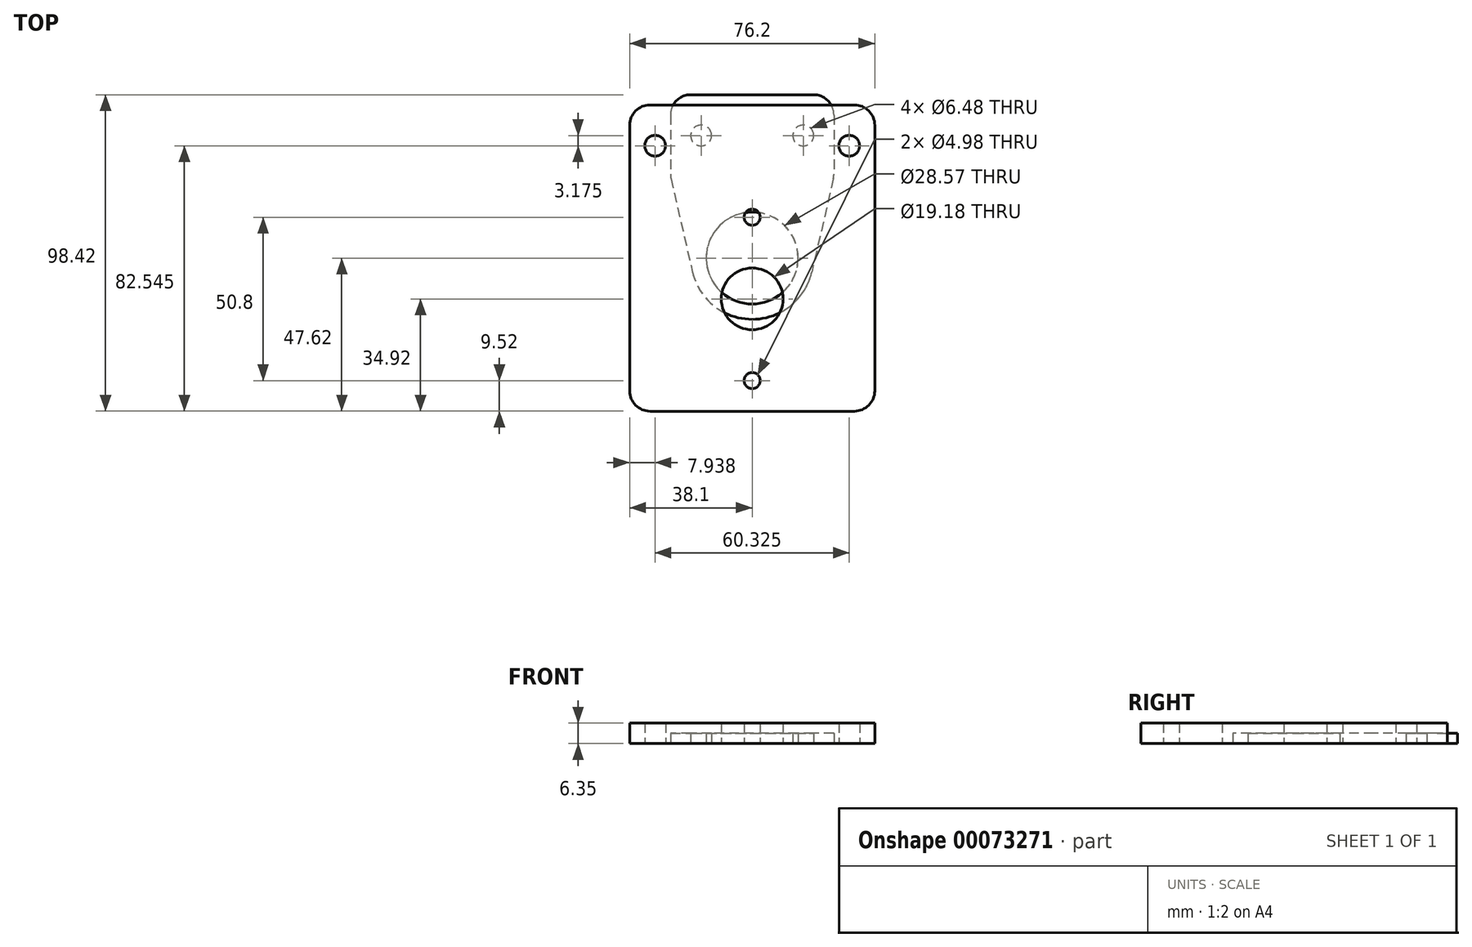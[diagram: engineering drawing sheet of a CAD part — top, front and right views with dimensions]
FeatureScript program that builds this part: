
annotation { "Feature Type Name" : "Feature", "Feature Type Description" : "" }
export const myFeature = defineFeature(function(context is Context, id is Id, definition is map)
    precondition{}
    {
        {
            var Q0;
            Q0=qCreatedBy(makeId("Top.planeOp"),FACE);
            var sketch = newSketch(context, id + "F0", { "sketchPlane" : qUnion([Q0])});
            skLineSegment(sketch, "E0.rect.bottom", {"start": v(38.1, 47.62) * mm, "end": v(-38.1, 47.62) * mm});
            skLineSegment(sketch, "E0.rect.top", {"start": v(38.1, -47.63) * mm, "end": v(-38.1, -47.63) * mm});
            skLineSegment(sketch, "E0.rect.left", {"start": v(38.1, 47.63) * mm, "end": v(38.1, -47.63) * mm});
            skLineSegment(sketch, "E0.rect.right", {"start": v(-38.1, 47.63) * mm, "end": v(-38.1, -47.63) * mm});
            skPoint(sketch, "E0.rect.middle", {"position": v(0, 0) * mm});
            skLineSegment(sketch, "E1", {"start": v(-38.1, 22.22) * mm, "end": v(38.1, 22.23) * mm, "construction": true});
            skLineSegment(sketch, "E2", {"start": v(0, 47.62) * mm, "end": v(0, -47.63) * mm, "construction": true});
            skLineSegment(sketch, "E3", {"start": v(-38.1, 34.92) * mm, "end": v(38.1, 34.92) * mm, "construction": true});
            skCircle(sketch, "E4", {"center": v(-30.16, 34.92) * mm, "radius": 3.24 * mm});
            skCircle(sketch, "E5", {"center": v(30.16, 34.92) * mm, "radius": 3.24 * mm});
            skCircle(sketch, "E6", {"center": v(0, -12.7) * mm, "radius": 9.59 * mm});
            skCircle(sketch, "E7", {"center": v(0, -12.7) * mm, "radius": 32.39 * mm, "construction": true});
            skCircle(sketch, "E8", {"center": v(0, -12.7) * mm, "radius": 25.4 * mm, "construction": true});
            skCircle(sketch, "E9", {"center": v(0, 12.7) * mm, "radius": 2.49 * mm});
            skCircle(sketch, "E10", {"center": v(0, -38.1) * mm, "radius": 2.49 * mm});
            skLineSegment(sketch, "E11", {"start": v(-32.39, -12.7) * mm, "end": v(32.39, -12.7) * mm, "construction": true});
            skSolve(sketch);
        }
        {
            var Q0;
            Q0=makeQuery(id+"F0.imprint","IMPRINT",FACE,{"disambiguationData":[TD([[makeQuery(id+"F0.imprint","IMPRINT",EDGE,{"derivedFrom":sQuery(id+"F0.wireOp",EDGE,"E0.rect.bottom")}),1.0]])]});
            extrude(context, id + "F1", {"entities" : qUnion([Q0]), "depth" : 6.35 * mm});
        }
        {
            var Q0;
            Q0=makeQuery(id+"F1.opExtrude","SWEPT_EDGE",EDGE,{"disambiguationData":[OSD([sQuery(id+"F0.wireOp",EDGE,"E0.rect.bottom"),sQuery(id+"F0.wireOp",EDGE,"E0.rect.right")])]});
            var Q1;
            Q1=makeQuery(id+"F1.opExtrude","SWEPT_EDGE",EDGE,{"disambiguationData":[OSD([sQuery(id+"F0.wireOp",EDGE,"E0.rect.top"),sQuery(id+"F0.wireOp",EDGE,"E0.rect.right")])]});
            var Q2;
            Q2=makeQuery(id+"F1.opExtrude","SWEPT_EDGE",EDGE,{"disambiguationData":[OSD([sQuery(id+"F0.wireOp",EDGE,"E0.rect.top"),sQuery(id+"F0.wireOp",EDGE,"E0.rect.left")])]});
            var Q3;
            Q3=makeQuery(id+"F1.opExtrude","SWEPT_EDGE",EDGE,{"disambiguationData":[OSD([sQuery(id+"F0.wireOp",EDGE,"E0.rect.bottom"),sQuery(id+"F0.wireOp",EDGE,"E0.rect.left")])]});
            fillet(context, id + "F2", {"entities" : qUnion([Q0, Q1, Q2, Q3]), "radius" : 6.35 * mm, "tangentPropagation" : true, "allowEdgeOverflow" : false});
        }
        {
            var Q0;
            Q0=qCreatedBy(makeId("Top.planeOp"),FACE);
            var sketch = newSketch(context, id + "F3", { "sketchPlane" : qUnion([Q0])});
            skCircle(sketch, "E12", {"center": v(0, 0) * mm, "radius": 14.29 * mm});
            skLineSegment(sketch, "E13.bottom", {"start": v(-25.4, 50.8) * mm, "end": v(25.4, 50.8) * mm});
            skLineSegment(sketch, "E13.left", {"start": v(-25.4, 50.8) * mm, "end": v(-25.4, 25.4) * mm});
            skLineSegment(sketch, "E13.right", {"start": v(25.4, 50.8) * mm, "end": v(25.4, 25.4) * mm});
            skLineSegment(sketch, "E14", {"start": v(0, 0) * mm, "end": v(0, 50.8) * mm, "construction": true});
            skCircle(sketch, "E15", {"center": v(-15.87, 38.1) * mm, "radius": 3.24 * mm});
            skCircle(sketch, "E16", {"center": v(15.87, 38.1) * mm, "radius": 3.24 * mm});
            skArc(sketch, "E17", {"start": v(-18.56, -4.28) * mm, "mid": v(0, -19.05) * mm, "end": v(18.56, -4.28) * mm});
            skLineSegment(sketch, "E18", {"start": v(25.4, 25.4) * mm, "end": v(18.56, -4.28) * mm});
            skLineSegment(sketch, "E19", {"start": v(-25.4, 25.4) * mm, "end": v(-18.56, -4.28) * mm});
            skSolve(sketch);
        }
        {
            var Q0;
            Q0=makeQuery(id+"F3.imprint","IMPRINT",FACE,{"disambiguationData":[TD([[makeQuery(id+"F3.imprint","IMPRINT",EDGE,{"derivedFrom":sQuery(id+"F3.wireOp",EDGE,"E12")}),-1.0]])]});
            extrude(context, id + "F4", {"entities" : qUnion([Q0]), "depth" : 3.17 * mm});
        }
        {
            var Q0;
            Q0=makeQuery(id+"F4.opExtrude","SWEPT_EDGE",EDGE,{"disambiguationData":[OSD([sQuery(id+"F3.wireOp",EDGE,"E13.bottom"),sQuery(id+"F3.wireOp",EDGE,"E13.right")])]});
            var Q1;
            Q1=makeQuery(id+"F4.opExtrude","SWEPT_EDGE",EDGE,{"disambiguationData":[OSD([sQuery(id+"F3.wireOp",EDGE,"E13.right"),sQuery(id+"F3.wireOp",EDGE,"E18")])]});
            var Q2;
            Q2=makeQuery(id+"F4.opExtrude","SWEPT_EDGE",EDGE,{"disambiguationData":[OSD([sQuery(id+"F3.wireOp",EDGE,"E13.left"),sQuery(id+"F3.wireOp",EDGE,"E19")])]});
            var Q3;
            Q3=makeQuery(id+"F4.opExtrude","SWEPT_EDGE",EDGE,{"disambiguationData":[OSD([sQuery(id+"F3.wireOp",EDGE,"E13.bottom"),sQuery(id+"F3.wireOp",EDGE,"E13.left")])]});
            fillet(context, id + "F5", {"entities" : qUnion([Q0, Q1, Q2, Q3]), "radius" : 6.35 * mm, "tangentPropagation" : true, "allowEdgeOverflow" : false});
        }
    });
